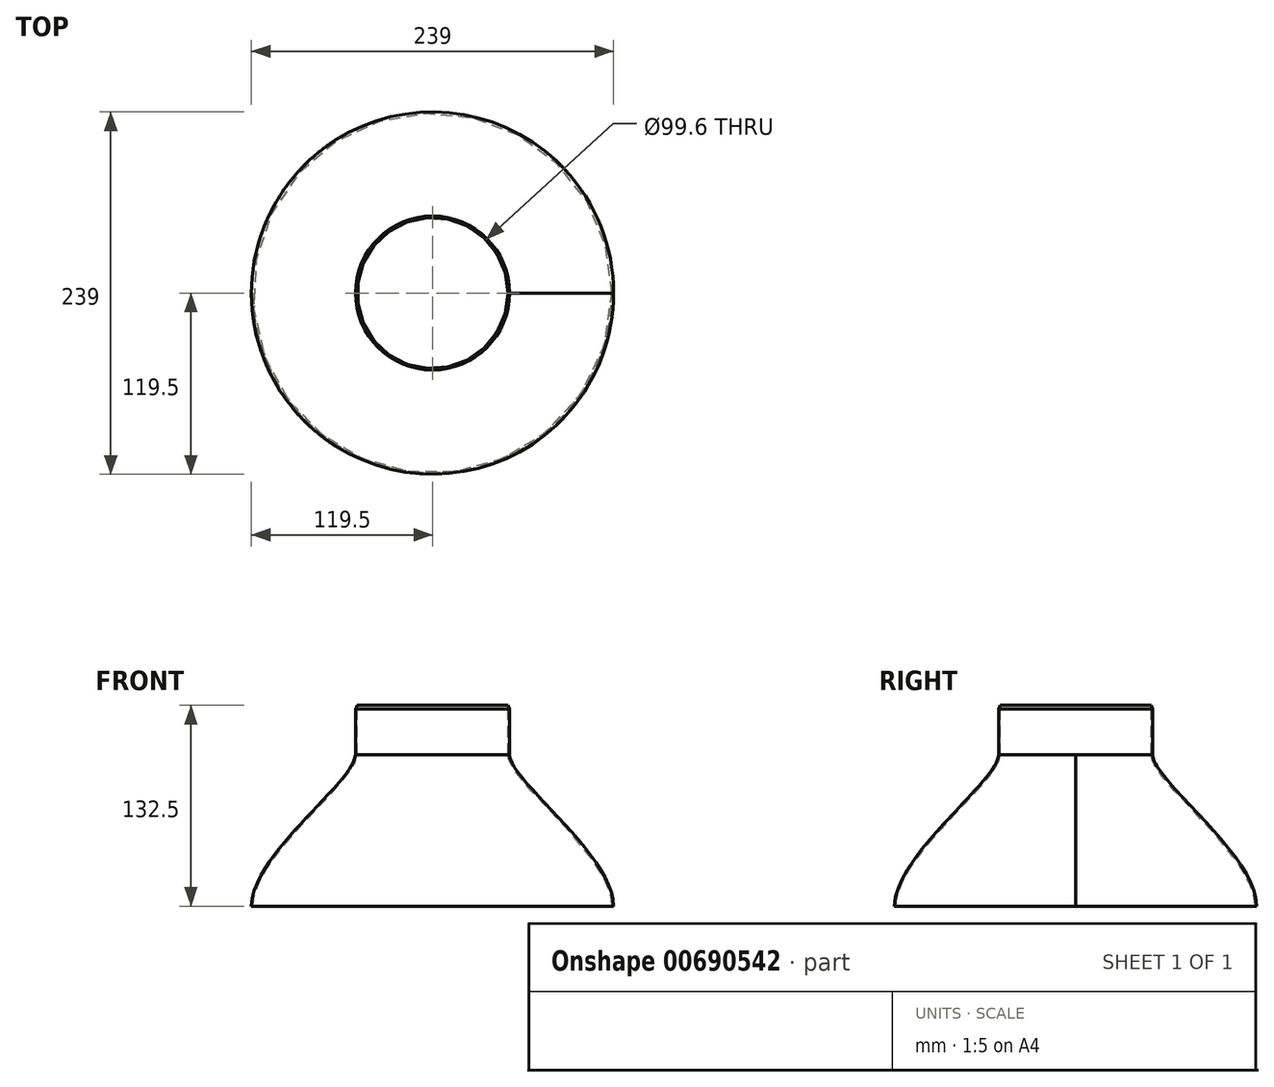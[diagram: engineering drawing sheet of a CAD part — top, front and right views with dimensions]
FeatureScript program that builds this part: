
annotation { "Feature Type Name" : "Feature", "Feature Type Description" : "" }
export const myFeature = defineFeature(function(context is Context, id is Id, definition is map)
    precondition{}
    {
        {
            var Q0;
            Q0=qCreatedBy(makeId("Front.planeOp"),FACE);
            var sketch = newSketch(context, id + "F0", { "sketchPlane" : qUnion([Q0])});
            skLineSegment(sketch, "E0", {"start": v(50.8, 0) * mm, "end": v(50.8, 30) * mm});
            skLineSegment(sketch, "E1", {"start": v(50.8, 30) * mm, "end": v(48.8, 35) * mm});
            skLineSegment(sketch, "E2", {"start": v(48.8, 35) * mm, "end": v(0, 35) * mm});
            skLineSegment(sketch, "E3", {"start": v(0, 35) * mm, "end": v(0, 0) * mm});
            skLineSegment(sketch, "E4", {"start": v(50.8, 0) * mm, "end": v(0, 0) * mm});
            skSolve(sketch);
        }
        {
            var Q0;
            Q0=makeQuery(id+"F0.imprint","IMPRINT",FACE,{"disambiguationData":[TD([[makeQuery(id+"F0.imprint","IMPRINT",EDGE,{"derivedFrom":sQuery(id+"F0.wireOp",EDGE,"E0")}),1.0]])]});
            var Q1;
            Q1=sQuery(id+"F0.wireOp",EDGE,"E3");
            revolve(context, id + "F1", {"entities" : qUnion([Q0]), "axis" : qUnion([Q1]), "revolveType" : RevolveType.FULL});
        }
        {
            var Q0;
            Q0=qCreatedBy(makeId("Top.planeOp"),FACE);
            cPlane(context, id + "F2", {"entities" : qUnion([Q0]), "cplaneType" : CPlaneType.OFFSET, "offset" : 100 * mm, "oppositeDirection" : true, "width" : 150 * mm, "height" : 150 * mm});
        }
        {
            var Q0;
            Q0=qCreatedBy(id+"F2.planeOp",FACE);
            var sketch = newSketch(context, id + "F3", { "sketchPlane" : qUnion([Q0])});
            skCircle(sketch, "E5", {"center": v(0, 0) * mm, "radius": 119.5 * mm});
            skSolve(sketch);
        }
        {
            var Q1;
            Q1=makeQuery(id+"F3.imprint","IMPRINT",FACE,{"disambiguationData":[TD([[makeQuery(id+"F3.imprint","IMPRINT",EDGE,{"derivedFrom":sQuery(id+"F3.wireOp",EDGE,"E5")}),1.0]])]});
            var Q2;
            Q2=makeQuery(id+"F1.opRevolve","SWEPT_FACE",FACE,{"disambiguationData":[OSD([sQuery(id+"F0.wireOp",EDGE,"E4")])]});
            loft(context, id + "F4", {"operationType" : NewBodyOperationType.ADD, "startCondition" : LoftEndDerivativeType.NORMAL_TO_PROFILE, "startMagnitude" : 1, "endCondition" : LoftEndDerivativeType.NORMAL_TO_PROFILE, "endMagnitude" : 0.5, "sheetProfilesArray" : [{ "sheetProfileEntities" : qUnion([Q1]) }, { "sheetProfileEntities" : qUnion([Q2]) }]});
        }
        {
            var Q0;
            Q0=makeQuery(id+"F1.opRevolve","SWEPT_FACE",FACE,{"disambiguationData":[OSD([sQuery(id+"F0.wireOp",EDGE,"E2")])]});
            var Q1;
            Q1=makeQuery(id+"F1.opRevolve","SWEPT_FACE",FACE,{"disambiguationData":[OSD([sQuery(id+"F0.wireOp",EDGE,"E1")])]});
            var Q2;
            Q2=makeQuery(id+"F4.opLoft","CAP_FACE",FACE,{"disambiguationData":[OSD([makeQuery(id+"F3.imprint","IMPRINT",FACE,{"disambiguationData":[TD([[makeQuery(id+"F3.imprint","IMPRINT",EDGE,{"derivedFrom":sQuery(id+"F3.wireOp",EDGE,"E5")}),1.0]])]})])],"isStart":true});
            shell(context, id + "F5", {"entities" : qUnion([Q0, Q1, Q2]), "thickness" : 1 * mm});
        }
    });
